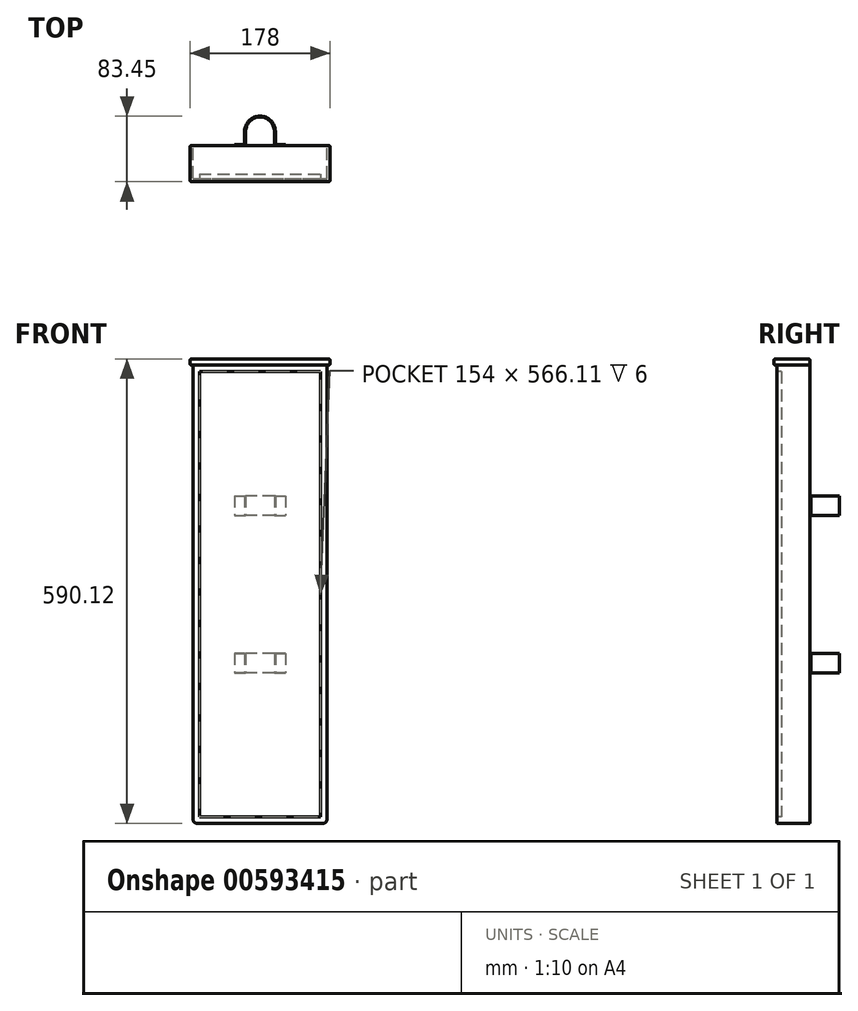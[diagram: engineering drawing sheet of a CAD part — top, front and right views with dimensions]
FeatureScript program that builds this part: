
annotation { "Feature Type Name" : "Feature", "Feature Type Description" : "" }
export const myFeature = defineFeature(function(context is Context, id is Id, definition is map)
    precondition{}
    {
        {
            var Q0;
            Q0=qCreatedBy(makeId("Front.planeOp"),FACE);
            var sketch = newSketch(context, id + "F0", { "sketchPlane" : qUnion([Q0])});
            skLineSegment(sketch, "E0.bottom", {"start": v(-77, 283.06) * mm, "end": v(77, 283.06) * mm});
            skLineSegment(sketch, "E0.top", {"start": v(-77, -283.06) * mm, "end": v(77, -283.06) * mm});
            skLineSegment(sketch, "E0.left", {"start": v(-77, 283.06) * mm, "end": v(-77, -283.06) * mm});
            skLineSegment(sketch, "E0.right", {"start": v(77, 283.06) * mm, "end": v(77, -283.06) * mm});
            skPoint(sketch, "E0.middle", {"position": v(0, 0) * mm});
            skLineSegment(sketch, "E1.bottom", {"start": v(-85, 291.06) * mm, "end": v(85, 291.06) * mm});
            skLineSegment(sketch, "E1.top", {"start": v(-85, -291.06) * mm, "end": v(85, -291.06) * mm});
            skLineSegment(sketch, "E1.left", {"start": v(-85, 291.06) * mm, "end": v(-85, -291.06) * mm});
            skLineSegment(sketch, "E1.right", {"start": v(85, 291.06) * mm, "end": v(85, -291.06) * mm});
            skLineSegment(sketch, "E2.top", {"start": v(-85, 325.06) * mm, "end": v(85, 325.06) * mm});
            skLineSegment(sketch, "E2.left", {"start": v(-85, 291.06) * mm, "end": v(-85, 325.06) * mm});
            skLineSegment(sketch, "E2.right", {"start": v(85, 291.06) * mm, "end": v(85, 325.06) * mm});
            skSolve(sketch);
        }
        {
            var Q0;
            Q0=qCreatedBy(makeId("Front.planeOp"),FACE);
            var sketch = newSketch(context, id + "F1", { "sketchPlane" : qUnion([Q0])});
            skLineSegment(sketch, "E3.bottom", {"start": v(-85, 291.06) * mm, "end": v(85, 291.06) * mm});
            skLineSegment(sketch, "E3.top", {"start": v(-85, -291.06) * mm, "end": v(85, -291.06) * mm});
            skLineSegment(sketch, "E3.left", {"start": v(-85, 291.06) * mm, "end": v(-85, -291.06) * mm});
            skLineSegment(sketch, "E3.right", {"start": v(85, 291.06) * mm, "end": v(85, -291.06) * mm});
            skSolve(sketch);
        }
        {
            var Q0;
            Q0 = qSketchRegion(id + "F1", true);
            extrude(context, id + "F2", {"entities" : qUnion([Q0]), "depth" : 42 * mm, "offsetDistance" : 25 * mm});
        }
        {
            var Q0;
            Q0=makeQuery(id+"F2.opExtrude","CAP_FACE",FACE,{"disambiguationData":[OSD([sQuery(id+"F1.wireOp",EDGE,"E3.bottom"),sQuery(id+"F1.wireOp",EDGE,"E3.top"),sQuery(id+"F1.wireOp",EDGE,"E3.left"),sQuery(id+"F1.wireOp",EDGE,"E3.right")])],"isStart":false});
            var sketch = newSketch(context, id + "F3", { "sketchPlane" : qUnion([Q0])});
            skLineSegment(sketch, "E4.bottom", {"start": v(-77, 283.06) * mm, "end": v(77, 283.06) * mm});
            skLineSegment(sketch, "E4.top", {"start": v(-77, -283.06) * mm, "end": v(77, -283.06) * mm});
            skLineSegment(sketch, "E4.left", {"start": v(-77, 283.06) * mm, "end": v(-77, -283.06) * mm});
            skLineSegment(sketch, "E4.right", {"start": v(77, 283.06) * mm, "end": v(77, -283.06) * mm});
            skSolve(sketch);
        }
        {
            var Q0;
            Q0 = qSketchRegion(id + "F3", true);
            extrude(context, id + "F4", {"entities" : qUnion([Q0]), "operationType" : NewBodyOperationType.REMOVE, "oppositeDirection" : true, "depth" : 6 * mm, "offsetDistance" : 25 * mm});
        }
        {
            var Q0;
            Q0=makeQuery(id+"F2.opExtrude","SWEPT_FACE",FACE,{"disambiguationData":[OSD([sQuery(id+"F1.wireOp",EDGE,"E3.left")])]});
            cPlane(context, id + "F5", {"entities" : qUnion([Q0]), "cplaneType" : CPlaneType.OFFSET, "offset" : 4 * mm, "width" : 150 * mm, "height" : 150 * mm});
        }
        {
            var Q0;
            Q0=makeQuery(id+"F2.opExtrude","SWEPT_FACE",FACE,{"disambiguationData":[OSD([sQuery(id+"F1.wireOp",EDGE,"E3.right")])]});
            cPlane(context, id + "F6", {"entities" : qUnion([Q0]), "cplaneType" : CPlaneType.OFFSET, "offset" : 4 * mm, "width" : 150 * mm, "height" : 150 * mm});
        }
        {
            var Q0;
            Q0=qCreatedBy(id+"F5.planeOp",FACE);
            var sketch = newSketch(context, id + "F7", { "sketchPlane" : qUnion([Q0])});
            skLineSegment(sketch, "E5.bottom", {"start": v(46, 291.06) * mm, "end": v(0, 291.06) * mm});
            skLineSegment(sketch, "E5.top", {"start": v(46, 299.06) * mm, "end": v(0, 299.06) * mm});
            skLineSegment(sketch, "E5.left", {"start": v(46, 291.06) * mm, "end": v(46, 299.06) * mm});
            skLineSegment(sketch, "E5.right", {"start": v(0, 291.06) * mm, "end": v(0, 299.06) * mm});
            skSolve(sketch);
        }
        {
            var Q0;
            Q0=makeQuery(id+"F2.opExtrude","SWEPT_EDGE",EDGE,{"disambiguationData":[OSD([sQuery(id+"F1.wireOp",EDGE,"E3.top"),sQuery(id+"F1.wireOp",EDGE,"E3.left")])]});
            var Q1;
            Q1=makeQuery(id+"F2.opExtrude","SWEPT_EDGE",EDGE,{"disambiguationData":[OSD([sQuery(id+"F1.wireOp",EDGE,"E3.top"),sQuery(id+"F1.wireOp",EDGE,"E3.right")])]});
            fillet(context, id + "F8", {"entities" : qUnion([Q0, Q1]), "radius" : 5 * mm, "tangentPropagation" : true, "allowEdgeOverflow" : false});
        }
        {
            var Q0;
            Q0=makeQuery(id+"F2.opExtrude","CAP_EDGE",EDGE,{"disambiguationData":[OSD([sQuery(id+"F1.wireOp",EDGE,"E3.left")])],"isStart":false});
            var Q1;
            Q1=makeQuery(id+"F4.boolean.opBoolean","COPY",EDGE,{"derivedFrom":makeQuery(id+"F4.opExtrude","CAP_EDGE",EDGE,{"disambiguationData":[OSD([sQuery(id+"F3.wireOp",EDGE,"E4.left")])],"isStart":true})});
            var Q2;
            Q2=makeQuery(id+"F4.boolean.opBoolean","COPY",EDGE,{"derivedFrom":makeQuery(id+"F4.opExtrude","CAP_EDGE",EDGE,{"disambiguationData":[OSD([sQuery(id+"F3.wireOp",EDGE,"E4.right")])],"isStart":true})});
            var Q3;
            Q3=makeQuery(id+"F2.opExtrude","CAP_EDGE",EDGE,{"disambiguationData":[OSD([sQuery(id+"F1.wireOp",EDGE,"E3.right")])],"isStart":false});
            var Q4;
            Q4=makeQuery(id+"F4.boolean.opBoolean","COPY",EDGE,{"derivedFrom":makeQuery(id+"F4.opExtrude","CAP_EDGE",EDGE,{"disambiguationData":[OSD([sQuery(id+"F3.wireOp",EDGE,"E4.top")])],"isStart":true})});
            var Q5;
            Q5=makeQuery(id+"F2.opExtrude","CAP_EDGE",EDGE,{"disambiguationData":[OSD([sQuery(id+"F1.wireOp",EDGE,"E3.right")])],"isStart":true});
            var Q6;
            Q6=makeQuery(id+"F2.opExtrude","CAP_EDGE",EDGE,{"disambiguationData":[OSD([sQuery(id+"F1.wireOp",EDGE,"E3.left")])],"isStart":true});
            var Q7;
            Q7=makeQuery(id+"F4.boolean.opBoolean","COPY",EDGE,{"derivedFrom":makeQuery(id+"F4.opExtrude","CAP_EDGE",EDGE,{"disambiguationData":[OSD([sQuery(id+"F3.wireOp",EDGE,"E4.bottom")])],"isStart":true})});
            fillet(context, id + "F9", {"entities" : qUnion([Q0, Q1, Q2, Q3, Q4, Q5, Q6, Q7]), "radius" : .8 * mm, "tangentPropagation" : true, "allowEdgeOverflow" : false});
        }
        {
            var Q0;
            Q0 = qSketchRegion(id + "F7", true);
            var Q1;
            Q1=qCreatedBy(id+"F6.planeOp",FACE);
            extrude(context, id + "F10", {"entities" : qUnion([Q0]), "operationType" : NewBodyOperationType.ADD, "endBound" : BoundingType.UP_TO_SURFACE, "oppositeDirection" : true, "depth" : 25 * mm, "endBoundEntityFace" : qUnion([Q1]), "offsetDistance" : 25 * mm});
        }
        {
            var Q0;
            Q0=makeQuery(id+"F10.opExtrude","SWEPT_FACE",FACE,{"disambiguationData":[OSD([sQuery(id+"F7.wireOp",EDGE,"E5.top")])]});
            var Q1;
            Q1=makeQuery(id+"F10.opExtrude","CAP_EDGE",EDGE,{"disambiguationData":[OSD([sQuery(id+"F7.wireOp",EDGE,"E5.left")])],"isStart":true});
            var Q2;
            Q2=makeQuery(id+"F10.opExtrude","CAP_EDGE",EDGE,{"disambiguationData":[OSD([sQuery(id+"F7.wireOp",EDGE,"E5.left")])],"isStart":false});
            var Q3;
            Q3=makeQuery(id+"F10.opExtrude","CAP_EDGE",EDGE,{"disambiguationData":[OSD([sQuery(id+"F7.wireOp",EDGE,"E5.right")])],"isStart":false});
            var Q4;
            Q4=makeQuery(id+"F10.opExtrude","CAP_EDGE",EDGE,{"disambiguationData":[OSD([sQuery(id+"F7.wireOp",EDGE,"E5.right")])],"isStart":true});
            var Q5;
            Q5=makeQuery(id+"F10.opExtrude","CAP_EDGE",EDGE,{"disambiguationData":[OSD([sQuery(id+"F7.wireOp",EDGE,"E5.bottom")])],"isStart":true});
            var Q6;
            Q6=makeQuery(id+"F10.opExtrude","SWEPT_EDGE",EDGE,{"disambiguationData":[OSD([sQuery(id+"F7.wireOp",EDGE,"E5.bottom"),sQuery(id+"F7.wireOp",EDGE,"E5.left")])]});
            var Q7;
            Q7=makeQuery(id+"F10.opExtrude","CAP_EDGE",EDGE,{"disambiguationData":[OSD([sQuery(id+"F7.wireOp",EDGE,"E5.bottom")])],"isStart":false});
            fillet(context, id + "F11", {"entities" : qUnion([Q0, Q1, Q2, Q3, Q4, Q5, Q6, Q7]), "radius" : 2 * mm, "tangentPropagation" : true, "allowEdgeOverflow" : false});
        }
        {
            var Q0;
            Q0=qCreatedBy(makeId("Top.planeOp"),FACE);
            cPlane(context, id + "F12", {"entities" : qUnion([Q0]), "cplaneType" : CPlaneType.OFFSET, "offset" : 100 * mm, "width" : 150 * mm, "height" : 150 * mm});
        }
        {
            var Q0;
            Q0=qCreatedBy(makeId("Top.planeOp"),FACE);
            cPlane(context, id + "F13", {"entities" : qUnion([Q0]), "cplaneType" : CPlaneType.OFFSET, "offset" : 100 * mm, "oppositeDirection" : true, "width" : 150 * mm, "height" : 150 * mm});
        }
        {
            var Q0;
            Q0=qCreatedBy(id+"F12.planeOp",FACE);
            var sketch = newSketch(context, id + "F14", { "sketchPlane" : qUnion([Q0])});
            skCircle(sketch, "E6", {"center": v(0, 18) * mm, "radius": 18 * mm, "construction": true});
            skLineSegment(sketch, "E7", {"start": v(-32.25, 0) * mm, "end": v(-32.25, 0) * mm});
            skLineSegment(sketch, "E8", {"start": v(-32.25, 0) * mm, "end": v(-18.25, 0) * mm});
            skLineSegment(sketch, "E9", {"start": v(-18.25, 0) * mm, "end": v(-18.25, 18) * mm});
            skArc(sketch, "E10", {"start": v(-18.25, 18) * mm, "mid": v(0, 36.25) * mm, "end": v(18.25, 18) * mm});
            skLineSegment(sketch, "E11", {"start": v(18.25, 18) * mm, "end": v(18.25, 0) * mm});
            skLineSegment(sketch, "E12", {"start": v(18.25, 0) * mm, "end": v(32.25, 0) * mm});
            skLineSegment(sketch, "E13.0", {"start": v(19.45, 1.2) * mm, "end": v(32.25, 1.2) * mm});
            skLineSegment(sketch, "E13.1", {"start": v(-32.25, 1.2) * mm, "end": v(-19.45, 1.2) * mm});
            skLineSegment(sketch, "E13.2", {"start": v(-19.45, 1.2) * mm, "end": v(-19.45, 18) * mm});
            skArc(sketch, "E13.3", {"start": v(-19.45, 18) * mm, "mid": v(0, 37.45) * mm, "end": v(19.45, 18) * mm});
            skLineSegment(sketch, "E13.4", {"start": v(19.45, 18) * mm, "end": v(19.45, 1.2) * mm});
            skLineSegment(sketch, "E14", {"start": v(-32.25, 1.2) * mm, "end": v(-32.25, 0) * mm});
            skLineSegment(sketch, "E15", {"start": v(32.25, 1.2) * mm, "end": v(32.25, 0) * mm});
            skSolve(sketch);
        }
        {
            var Q0;
            Q0 = qSketchRegion(id + "F14", true);
            extrude(context, id + "F15", {"entities" : qUnion([Q0]), "operationType" : NewBodyOperationType.ADD, "depth" : 25 * mm, "offsetDistance" : 25 * mm});
        }
        {
            var Q0;
            Q0=qCreatedBy(id+"F13.planeOp",FACE);
            var sketch = newSketch(context, id + "F16", { "sketchPlane" : qUnion([Q0])});
            skLineSegment(sketch, "E16.0.0", {"start": v(19.45, 1.2) * mm, "end": v(19.45, 18) * mm});
            skArc(sketch, "E16.0.1", {"start": v(19.45, 18) * mm, "mid": v(0, 37.45) * mm, "end": v(-19.45, 18) * mm});
            skLineSegment(sketch, "E16.0.2", {"start": v(-19.45, 18) * mm, "end": v(-19.45, 1.2) * mm});
            skLineSegment(sketch, "E16.0.3", {"start": v(-19.45, 1.2) * mm, "end": v(-32.25, 1.2) * mm});
            skLineSegment(sketch, "E16.0.4", {"start": v(-32.25, 1.2) * mm, "end": v(-32.25, 0) * mm});
            skLineSegment(sketch, "E16.0.5", {"start": v(-32.25, 0) * mm, "end": v(-18.25, 0) * mm});
            skLineSegment(sketch, "E16.0.6", {"start": v(-18.25, 0) * mm, "end": v(-18.25, 18) * mm});
            skArc(sketch, "E16.0.7", {"start": v(-18.25, 18) * mm, "mid": v(0, 36.25) * mm, "end": v(18.25, 18) * mm});
            skLineSegment(sketch, "E16.0.8", {"start": v(18.25, 18) * mm, "end": v(18.25, 0) * mm});
            skLineSegment(sketch, "E16.0.9", {"start": v(18.25, 0) * mm, "end": v(32.25, 0) * mm});
            skLineSegment(sketch, "E16.0.10", {"start": v(32.25, 0) * mm, "end": v(32.25, 1.2) * mm});
            skLineSegment(sketch, "E16.0.11", {"start": v(32.25, 1.2) * mm, "end": v(19.45, 1.2) * mm});
            skSolve(sketch);
        }
        {
            var Q0;
            Q0 = qSketchRegion(id + "F16", true);
            extrude(context, id + "F17", {"entities" : qUnion([Q0]), "operationType" : NewBodyOperationType.ADD, "depth" : 25 * mm, "offsetDistance" : 25 * mm});
        }
    });
